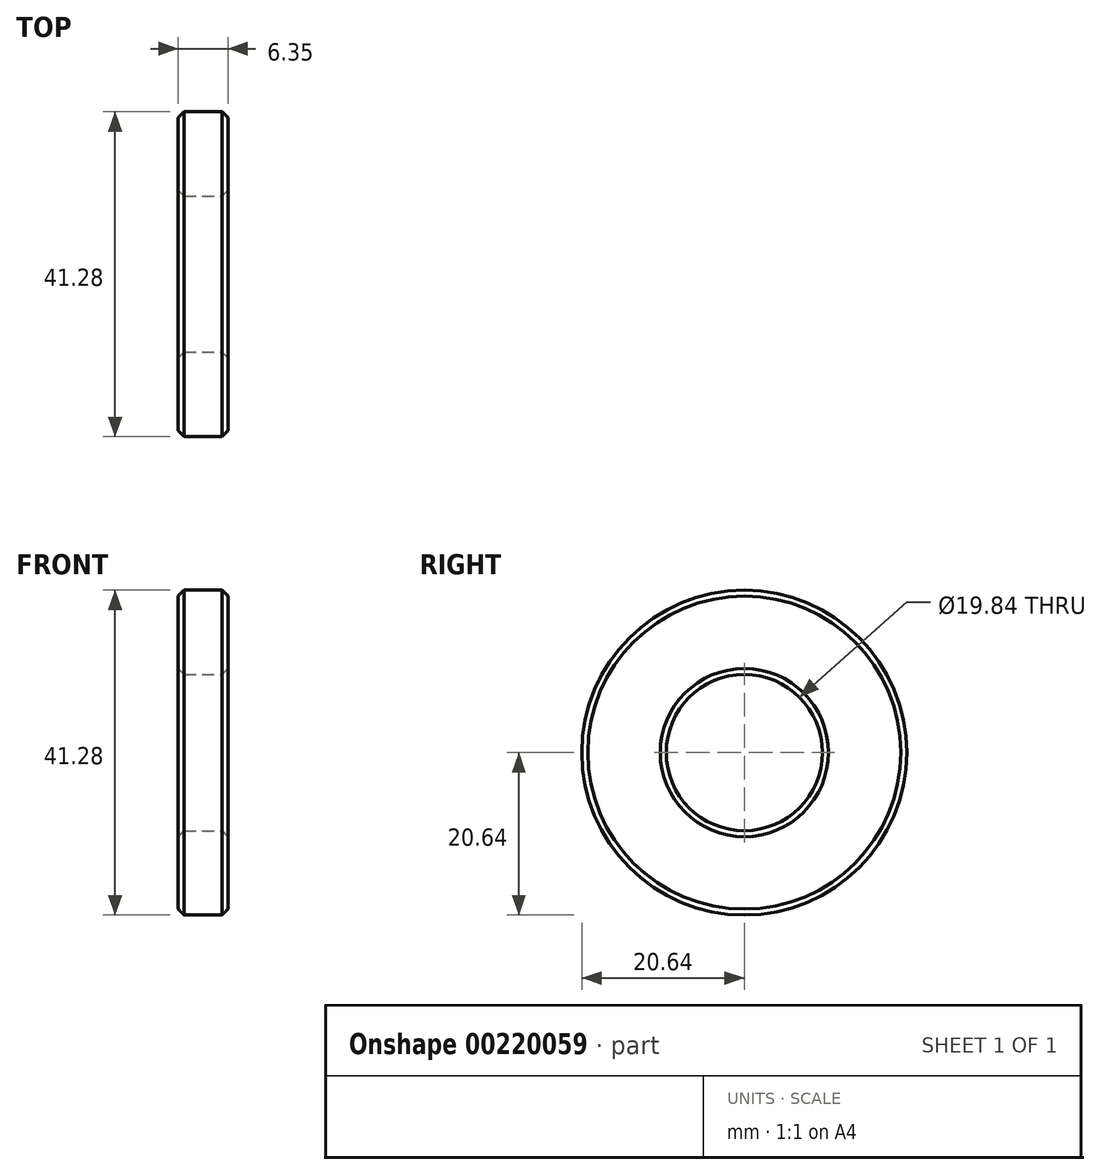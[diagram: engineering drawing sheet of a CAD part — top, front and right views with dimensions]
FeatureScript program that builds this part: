
annotation { "Feature Type Name" : "Feature", "Feature Type Description" : "" }
export const myFeature = defineFeature(function(context is Context, id is Id, definition is map)
    precondition{}
    {
        {
            var Q0;
            Q0=qCreatedBy(makeId("Right.planeOp"),FACE);
            var sketch = newSketch(context, id + "F0", { "sketchPlane" : qUnion([Q0])});
            skCircle(sketch, "E0", {"center": v(0, 0) * mm, "radius": 20.64 * mm});
            skCircle(sketch, "E1", {"center": v(0, 0) * mm, "radius": 9.92 * mm});
            skSolve(sketch);
        }
        {
            var Q0;
            Q0 = qSketchRegion(id + "F0", true);
            extrude(context, id + "F1", {"entities" : qUnion([Q0]), "oppositeDirection" : true, "depth" : 6.35 * mm});
        }
        {
            var Q0;
            Q0=makeQuery(id+"F1.opExtrude","CAP_EDGE",EDGE,{"disambiguationData":[OSD([sQuery(id+"F0.wireOp",EDGE,"E0")])],"isStart":true});
            var Q1;
            Q1=makeQuery(id+"F1.opExtrude","CAP_EDGE",EDGE,{"disambiguationData":[OSD([sQuery(id+"F0.wireOp",EDGE,"E0")])],"isStart":false});
            var Q2;
            Q2=makeQuery(id+"F1.opExtrude","CAP_EDGE",EDGE,{"disambiguationData":[OSD([sQuery(id+"F0.wireOp",EDGE,"E1")])],"isStart":true});
            var Q3;
            Q3=makeQuery(id+"F1.opExtrude","CAP_EDGE",EDGE,{"disambiguationData":[OSD([sQuery(id+"F0.wireOp",EDGE,"E1")])],"isStart":false});
            chamfer(context, id + "F2", {"entities" : qUnion([Q0, Q1, Q2, Q3]), "width" : 0.76 * mm, "tangentPropagation" : true});
        }
    });
